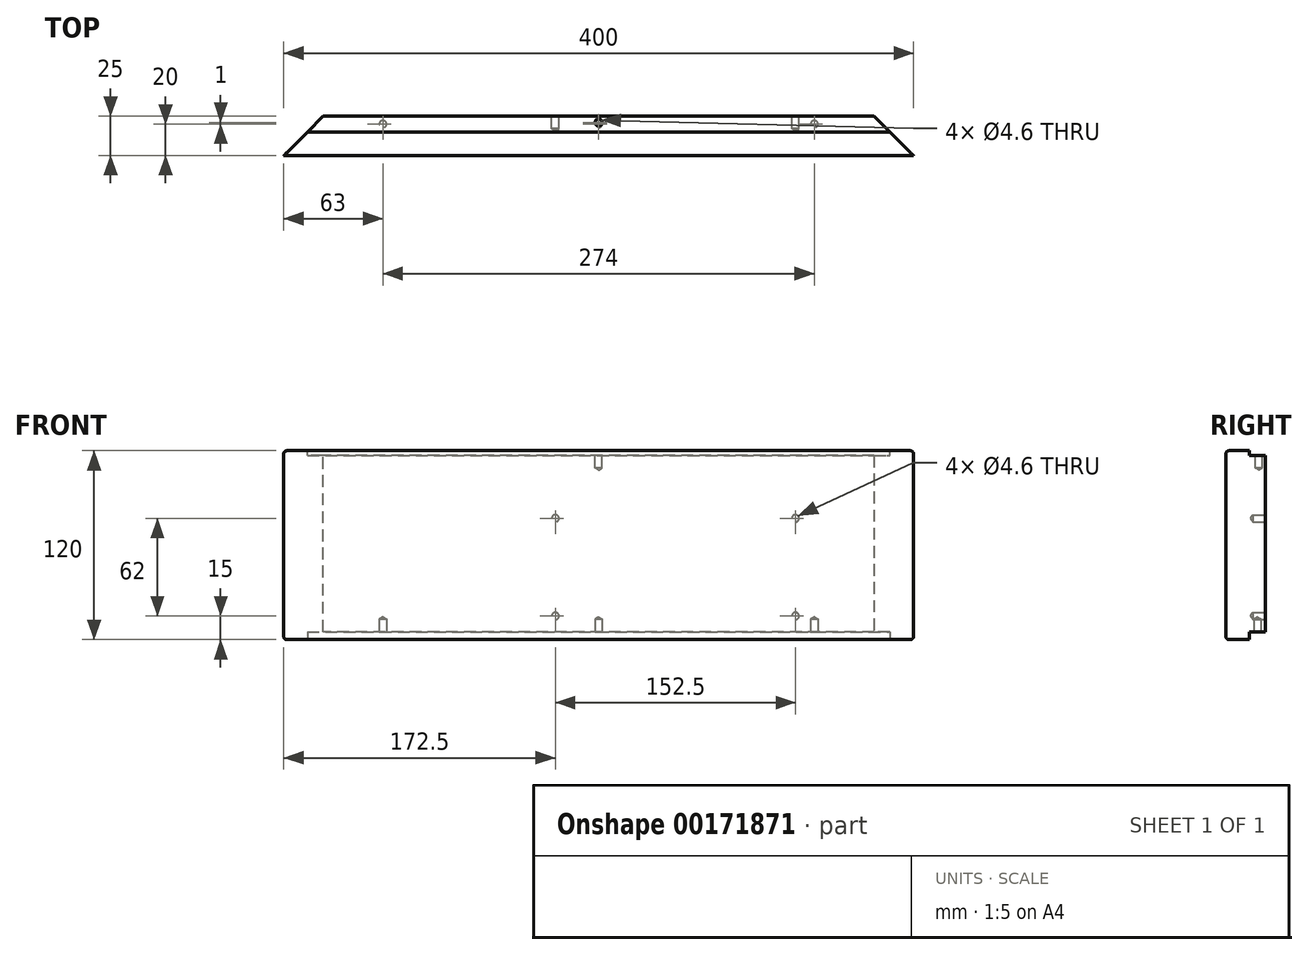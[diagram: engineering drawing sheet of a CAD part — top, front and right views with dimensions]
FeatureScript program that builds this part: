
annotation { "Feature Type Name" : "Feature", "Feature Type Description" : "" }
export const myFeature = defineFeature(function(context is Context, id is Id, definition is map)
    precondition{}
    {
        {
            var Q0;
            Q0=qCreatedBy(makeId("Front.planeOp"),FACE);
            var sketch = newSketch(context, id + "F0", { "sketchPlane" : qUnion([Q0])});
            skLineSegment(sketch, "E0.bottom", {"start": v(200, -60) * mm, "end": v(-200, -60) * mm});
            skLineSegment(sketch, "E0.top", {"start": v(200, 60) * mm, "end": v(-200, 60) * mm});
            skLineSegment(sketch, "E0.left", {"start": v(200, -60) * mm, "end": v(200, 60) * mm});
            skLineSegment(sketch, "E0.right", {"start": v(-200, -60) * mm, "end": v(-200, 60) * mm});
            skPoint(sketch, "E0.middle", {"position": v(0, 0) * mm});
            skSolve(sketch);
        }
        {
            var Q0;
            Q0=makeQuery(id+"F0.imprint","IMPRINT",FACE,{"disambiguationData":[TD([[makeQuery(id+"F0.imprint","IMPRINT",EDGE,{"derivedFrom":sQuery(id+"F0.wireOp",EDGE,"E0.bottom")}),-1.0]])]});
            extrude(context, id + "F1", {"entities" : qUnion([Q0]), "depth" : 25 * mm});
        }
        {
            var Q0;
            Q0=makeQuery(id+"F1.opExtrude","CAP_EDGE",EDGE,{"disambiguationData":[OSD([sQuery(id+"F0.wireOp",EDGE,"E0.right")])],"isStart":true});
            var Q1;
            Q1=makeQuery(id+"F1.opExtrude","CAP_EDGE",EDGE,{"disambiguationData":[OSD([sQuery(id+"F0.wireOp",EDGE,"E0.left")])],"isStart":true});
            chamfer(context, id + "F2", {"entities" : qUnion([Q0, Q1]), "width" : 25 * mm, "tangentPropagation" : true});
        }
        {
            var Q0;
            Q0=makeQuery(id+"F1.opExtrude","SWEPT_FACE",FACE,{"disambiguationData":[OSD([sQuery(id+"F0.wireOp",EDGE,"E0.top")])]});
            var sketch = newSketch(context, id + "F3", { "sketchPlane" : qUnion([Q0])});
            skLineSegment(sketch, "E1", {"start": v(-185, -10) * mm, "end": v(185, -10) * mm});
            skSolve(sketch);
        }
        {
            var Q0;
            {var subQ0=sQuery(id+"F3.wireOp",EDGE,"E1");Q0=makeQuery(id+"F3.imprint","IMPRINT",FACE,{"disambiguationData":[TD([[makeQuery(id+"F3.imprint","IMPRINT",EDGE,{"derivedFrom":subQ0}),1.0]])]});}
            extrude(context, id + "F4", {"entities" : qUnion([Q0]), "operationType" : NewBodyOperationType.REMOVE, "oppositeDirection" : true, "depth" : 3 * mm});
        }
        {
            var Q0;
            Q0=makeQuery(id+"F1.opExtrude","SWEPT_FACE",FACE,{"disambiguationData":[OSD([sQuery(id+"F0.wireOp",EDGE,"E0.bottom")])]});
            var sketch = newSketch(context, id + "F5", { "sketchPlane" : qUnion([Q0])});
            skLineSegment(sketch, "E2", {"start": v(-185, 10) * mm, "end": v(185, 10) * mm});
            skSolve(sketch);
        }
        {
            var Q0;
            {var subQ0=sQuery(id+"F5.wireOp",EDGE,"E2");Q0=makeQuery(id+"F5.imprint","IMPRINT",FACE,{"disambiguationData":[TD([[makeQuery(id+"F5.imprint","IMPRINT",EDGE,{"derivedFrom":subQ0}),-1.0]])]});}
            extrude(context, id + "F6", {"entities" : qUnion([Q0]), "operationType" : NewBodyOperationType.REMOVE, "oppositeDirection" : true, "depth" : 5 * mm});
        }
        {
            var Q0;
            Q0=makeQuery(id+"F4.boolean.opBoolean","COPY",FACE,{"derivedFrom":makeQuery(id+"F4.opExtrude","CAP_FACE",FACE,{"disambiguationData":[OSD([sQuery(id+"F0.wireOp",EDGE,"E0.top"),sQuery(id+"F0.wireOp",EDGE,"E0.left"),sQuery(id+"F0.wireOp",EDGE,"E0.right"),sQuery(id+"F3.wireOp",EDGE,"E1")])],"isStart":false})});
            var sketch = newSketch(context, id + "F7", { "sketchPlane" : qUnion([Q0])});
            skLineSegment(sketch, "E3", {"start": v(-176.3, -4) * mm, "end": v(171.3, -4) * mm, "construction": true});
            skPoint(sketch, "E3.endSnap0", {"position": v(161, -4) * mm});
            skLineSegment(sketch, "E4", {"start": v(0, 9.88) * mm, "end": v(0, -18.63) * mm, "construction": true});
            skPoint(sketch, "E5", {"position": v(0, -4) * mm});
            skSolve(sketch);
        }
        {
            var Q0;
            Q0=sQuery(id+"F7.wireOp",VERTEX,"E5");
            var Q1;
            Q1=makeQuery(id+"F1.opExtrude","SWEPT_BODY",BODY,{"disambiguationData":[OSD([sQuery(id+"F0.wireOp",EDGE,"E0.bottom"),sQuery(id+"F0.wireOp",EDGE,"E0.top"),sQuery(id+"F0.wireOp",EDGE,"E0.left"),sQuery(id+"F0.wireOp",EDGE,"E0.right")])]});
            hole(context, id + "F8", {"style" : HoleStyle.SIMPLE, "endStyle" : HoleEndStyle.BLIND, "holeDiameter" : 4.6 * mm, "holeDepth" : 8 * mm, "startFromSketch" : true, "locations" : qUnion([Q0]), "scope" : qUnion([Q1])});
        }
        {
            var Q0;
            Q0=makeQuery(id+"F6.boolean.opBoolean","COPY",FACE,{"derivedFrom":makeQuery(id+"F6.opExtrude","CAP_FACE",FACE,{"disambiguationData":[OSD([sQuery(id+"F0.wireOp",EDGE,"E0.bottom"),sQuery(id+"F0.wireOp",EDGE,"E0.left"),sQuery(id+"F0.wireOp",EDGE,"E0.right"),sQuery(id+"F5.wireOp",EDGE,"E2")])],"isStart":false})});
            var sketch = newSketch(context, id + "F9", { "sketchPlane" : qUnion([Q0])});
            skLineSegment(sketch, "E6", {"start": v(-174.3, 5) * mm, "end": v(174.8, 5) * mm, "construction": true});
            skLineSegment(sketch, "E7", {"start": v(0, 29.38) * mm, "end": v(0, -11.13) * mm, "construction": true});
            skPoint(sketch, "E7.endSnap0", {"position": v(0, 0) * mm});
            skLineSegment(sketch, "E8", {"start": v(137, 21.38) * mm, "end": v(137, -13.88) * mm, "construction": true});
            skLineSegment(sketch, "E9", {"start": v(-137, 23.63) * mm, "end": v(-137, -11.13) * mm, "construction": true});
            skPoint(sketch, "E10", {"position": v(-137, 5) * mm});
            skPoint(sketch, "E11", {"position": v(0, 5) * mm});
            skPoint(sketch, "E12", {"position": v(137, 5) * mm});
            skSolve(sketch);
        }
        {
            var Q0;
            Q0=sQuery(id+"F9.wireOp",VERTEX,"E10");
            var Q1;
            Q1=sQuery(id+"F9.wireOp",VERTEX,"E11");
            var Q2;
            Q2=sQuery(id+"F9.wireOp",VERTEX,"E12");
            var Q3;
            Q3=makeQuery(id+"F1.opExtrude","SWEPT_BODY",BODY,{"disambiguationData":[OSD([sQuery(id+"F0.wireOp",EDGE,"E0.bottom"),sQuery(id+"F0.wireOp",EDGE,"E0.top"),sQuery(id+"F0.wireOp",EDGE,"E0.left"),sQuery(id+"F0.wireOp",EDGE,"E0.right")])]});
            hole(context, id + "F10", {"style" : HoleStyle.SIMPLE, "endStyle" : HoleEndStyle.BLIND, "holeDiameter" : 4.6 * mm, "holeDepth" : 8 * mm, "startFromSketch" : true, "locations" : qUnion([Q0, Q1, Q2]), "scope" : qUnion([Q3])});
        }
        {
            var Q0;
            Q0=makeQuery(id+"F1.opExtrude","CAP_EDGE",EDGE,{"disambiguationData":[OSD([sQuery(id+"F0.wireOp",EDGE,"E0.top")])],"isStart":false});
            var Q1;
            Q1=makeQuery(id+"F1.opExtrude","CAP_EDGE",EDGE,{"disambiguationData":[OSD([sQuery(id+"F0.wireOp",EDGE,"E0.bottom")])],"isStart":false});
            fillet(context, id + "F11", {"entities" : qUnion([Q0, Q1]), "radius" : 2 * mm, "tangentPropagation" : true, "allowEdgeOverflow" : false});
        }
        {
            var Q0;
            Q0=makeQuery(id+"F0.imprint","IMPRINT",FACE,{"disambiguationData":[TD([[makeQuery(id+"F0.imprint","IMPRINT",EDGE,{"derivedFrom":sQuery(id+"F0.wireOp",EDGE,"E0.bottom")}),-1.0]])]});
            var sketch = newSketch(context, id + "F12", { "sketchPlane" : qUnion([Q0])});
            skLineSegment(sketch, "E13", {"start": v(126.33, -45) * mm, "end": v(-140.98, -45) * mm, "construction": true});
            skLineSegment(sketch, "E14", {"start": v(117.5, 17) * mm, "end": v(-137.2, 17) * mm, "construction": true});
            skLineSegment(sketch, "E15", {"start": v(-27.5, 23.62) * mm, "end": v(-27.5, -47.11) * mm, "construction": true});
            skLineSegment(sketch, "E16", {"start": v(125, 18.7) * mm, "end": v(125, -47.94) * mm, "construction": true});
            skPoint(sketch, "E17", {"position": v(125, 17) * mm});
            skPoint(sketch, "E18", {"position": v(125, -45) * mm});
            skPoint(sketch, "E19", {"position": v(-27.5, 17) * mm});
            skPoint(sketch, "E20", {"position": v(-27.5, -45) * mm});
            skSolve(sketch);
        }
        {
            var Q0;
            Q0=sQuery(id+"F12.wireOp",VERTEX,"E17");
            var Q1;
            Q1=sQuery(id+"F12.wireOp",VERTEX,"E19");
            var Q2;
            Q2=sQuery(id+"F12.wireOp",VERTEX,"E20");
            var Q3;
            Q3=sQuery(id+"F12.wireOp",VERTEX,"E18");
            var Q4;
            Q4=makeQuery(id+"F1.opExtrude","SWEPT_BODY",BODY,{"disambiguationData":[OSD([sQuery(id+"F0.wireOp",EDGE,"E0.bottom"),sQuery(id+"F0.wireOp",EDGE,"E0.top"),sQuery(id+"F0.wireOp",EDGE,"E0.left"),sQuery(id+"F0.wireOp",EDGE,"E0.right")])]});
            hole(context, id + "F13", {"style" : HoleStyle.SIMPLE, "endStyle" : HoleEndStyle.BLIND, "oppositeDirection" : true, "holeDiameter" : 4.6 * mm, "holeDepth" : 8 * mm, "startFromSketch" : true, "locations" : qUnion([Q0, Q1, Q2, Q3]), "scope" : qUnion([Q4])});
        }
    });
